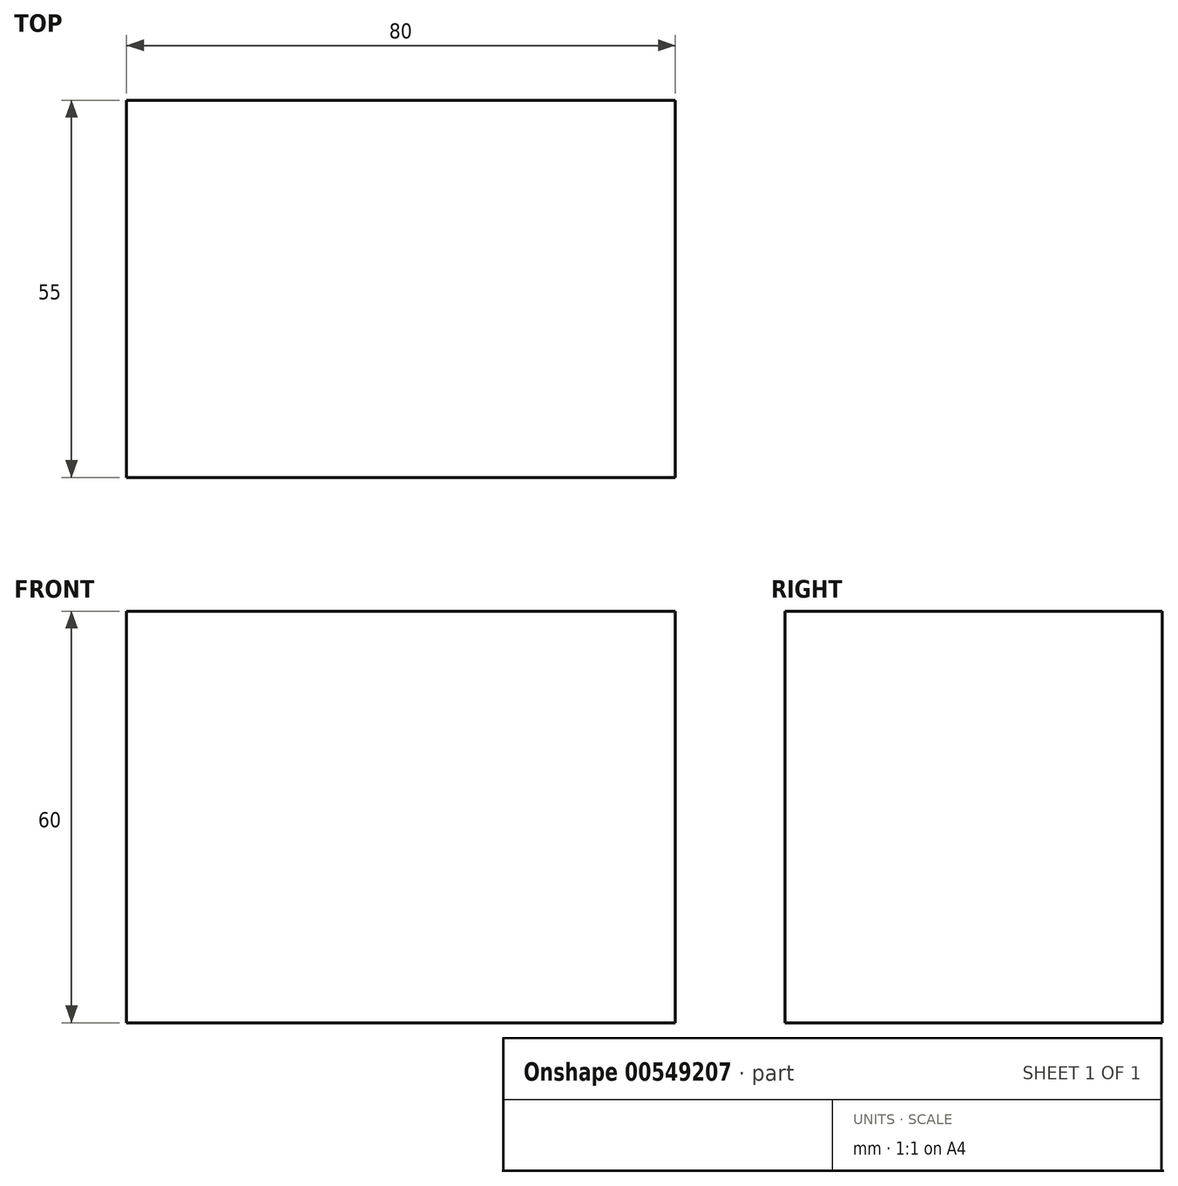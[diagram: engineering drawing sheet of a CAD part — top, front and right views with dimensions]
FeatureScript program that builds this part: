
annotation { "Feature Type Name" : "Feature", "Feature Type Description" : "" }
export const myFeature = defineFeature(function(context is Context, id is Id, definition is map)
    precondition{}
    {
        {
            var Q0;
            Q0=qCreatedBy(makeId("Front.planeOp"),FACE);
            var sketch = newSketch(context, id + "F0", { "sketchPlane" : qUnion([Q0])});
            skLineSegment(sketch, "E0", {"start": v(-44.53, 32.77) * mm, "end": v(35.47, 32.77) * mm});
            skLineSegment(sketch, "E1", {"start": v(35.47, 32.77) * mm, "end": v(35.47, -27.23) * mm});
            skLineSegment(sketch, "E2", {"start": v(35.47, -27.23) * mm, "end": v(-44.53, -27.23) * mm});
            skLineSegment(sketch, "E3", {"start": v(-44.53, -27.23) * mm, "end": v(-44.53, 32.77) * mm});
            skSolve(sketch);
        }
        {
            var Q0;
            Q0=makeQuery(id+"F0.imprint","IMPRINT",FACE,{"disambiguationData":[TD([[makeQuery(id+"F0.imprint","IMPRINT",EDGE,{"derivedFrom":sQuery(id+"F0.wireOp",EDGE,"E0")}),-1.0]])]});
            extrude(context, id + "F1", {"entities" : qUnion([Q0]), "endBound" : BoundingType.SYMMETRIC, "depth" : 55 * mm, "offsetDistance" : 25 * mm});
        }
    });
